# Revit family: Shower_Wall_Set-American_Standard-Studio-2946.SW_Series
name_source: partatom
category: Specialty Equipment
revit_build: Autodesk Revit 2018 (Build: 20170223_1515(x64)
units: mm (PartAtom-declared; Revit-internal decimal feet)

## family parameters
Always vertical = No
Cut with Voids When Loaded = No
OmniClass Number = 23.45.05.14.11.14
OmniClass Title = Bath Panels
Part Type = Normal
Room Calculation Point = No
Round Connector Dimension = Use Diameter
Shared = Yes
Work Plane-Based = Yes

## types (1)
- 2946SW.011
    Assembly Code = D2010710
    Default Elevation = 0"
    Description = Studio® 60 x 32 x 72-Inch Shower Wall Set
    Door Opening Length = 57 3/4"
    Finish = Polystyrene-American Standard-011- Arctic
    Height = 72"
    IAPMO Compliance = Meets or Exceeds CSA B45.5-11/IAPMO Z124-2011 for Plastic Showers
    Installation Type = Floor Mounted
    Length = 60"
    Manufacturer = American Standard
    Material = Polystyrene-American Standard-011- Arctic
    Model = 2946SW.011
    Product Documentation Link = https://americanstandard.box.com
    Product Page URL = https://www.americanstandard-us.com
    Revised Date = 01/25/2022
    Shelf Depth = 4 1/2"
    URL = http://www.americanstandard-us.com
    Warranty Information = Limited Lifetime warranty
    Width = 32"
    cUPC Compliant = Yes

## geometry (parser evidence)
native form markers: Sweep x2
no freeform markers — native parametric forms only
